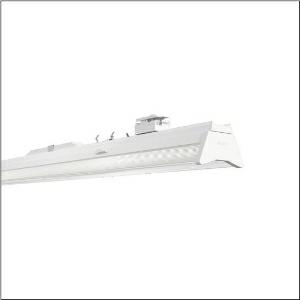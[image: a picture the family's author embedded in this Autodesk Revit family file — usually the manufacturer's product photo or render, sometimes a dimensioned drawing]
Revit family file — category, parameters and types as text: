
# Revit family: licross_21_performance_mo_52td16vn455g
name_source: partatom
category: Lighting Fixtures
units: mm (PartAtom-declared; Revit-internal decimal feet)

## family parameters
Cut with Voids When Loaded = No
Host = Face
Light Source = No
Part Type = Normal
Room Calculation Point = No
Round Connector Dimension = Use Diameter
Shared = No

## types (1)
- --- (1 x LED, 5500 lm, 30 W, 4000K)
    Apparent Load = 30 VA
    CIE Flux Codes = 66 88 96 79 100
    Color Rendering = 80
    Color Temperature = 4000K
    Default Elevation = 1800 mm
    Description = Licross 21 Performance MO, luminaire insert, of sheet steel, galvanised, coil coated, white, length: 1.500mm, width: 120mm, height: 123mm, LED rated luminous flux: 5.500lm, light colour: 840, SDCM (Standard Deviation of Colour Matching)MacAdam ≤ 3 SDCM (initial), control gear: DALI 2, CLO, with plug, 5-pole, with phase selection, mains connection: 220..240V, AC, 50/60Hz, start of lifetime: 30W, end of service life: 36W, internal wiring halogen-free, primary light control with lens, of plastic, primary optical cover: cover, of PMMA, light emission: direct/indirect distribution, primary light characteristic: symmetric, protection rating (complete): IP54, insulation class (complete): insulation class I (protective earthing), certification: CE, ENEC, VDE, UKCA, protection symbol: D if used in an environment with non-conductive dust loads with corresponding accessories, impact resistance: IK06, permissible ambient temperature for indoor applications: -25..+50°C, corresponds to IFS (International Featured Standards) requirements for safety and quality in the food industry, reducing of maximum allowable ambient temperature of 5°C with ceiling mounting, LABS conformity tested according to VDMA 24364:2018-05, The light source and the operating device comply with the requirements of the Ecodesign Regulation (EU) 2019/2020 and are replaceable in accordance with this regulation, packaging unit: 1 piece
    Height = 114 mm
    Lamp = 1 x LED
    Lamp Light Flux = 5500 lm
    Lamp Power = 30 W
    Lamp count = 1
    Length = 1500 mm
    Luminous efficacy = 183 lm/W
    Manufacturer = Siteco
    ModVariant = No
    Model = 52TD16VN455G
    Mounting Place = Ceiling
    Mounting Type = Pendant
    Number of Poles = 1
    OnlyDefault = Yes
    Power Factor = 1
    Product Name = Licross 21 Performance MO
    Product group = luminaire insert | ceiling pendant
    ProductGroupID = 901
    Protection Class = Protection class I
    Protection Degree = IP 54
    RLX_Detail_Level = 1
    RLX_Emergency_Light_Flux = 0 lm
    RLX_Emergency_Type = 0
    RLX_Emergency_Type_DB = No
    RlxData = <blob elided: 33697 chars, md5=c53253e0>
    Socket = socket
    Standby Power = 0 W
    System Light Flux = 5500 lm
    System Power = 30 W
    Type Comments = factory setting: luminous flux: 100 % | dim-lin: 254 | 203 mA
    Type Image = l_1256138.jpg
    URL = http://relux.com
    VarID = @adj_087993
    Voltage = 0 V
    Weight = 0.00 kg
    Width = 120 mm

## geometry (parser evidence)
native form markers: Blend x4, Sweep x12
no freeform markers — native parametric forms only
